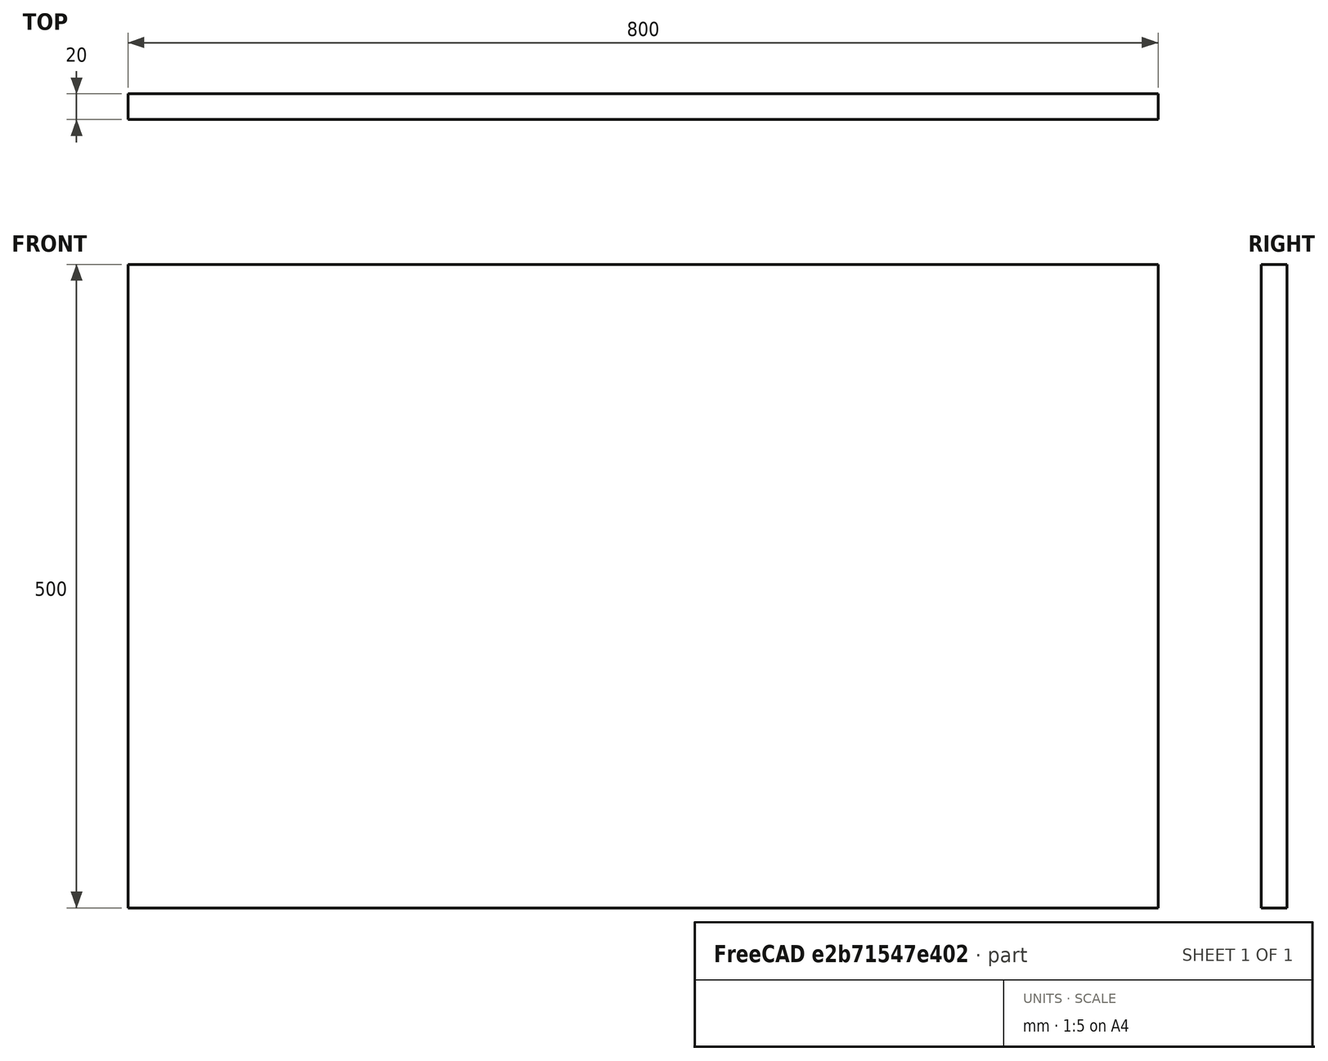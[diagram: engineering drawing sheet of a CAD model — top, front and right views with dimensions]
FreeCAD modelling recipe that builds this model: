
FCSTD DOCUMENT  (FreeCAD 0.20R29603 (Git))
Label: PlatteHinten
License: All rights reserved
LicenseURL: http://en.wikipedia.org/wiki/All_rights_reserved
objects: Sketcher::SketchObject×1, PartDesign::Pad×1, PartDesign::Body×1
note: 4 computed .brp shape members not serialized (recipe doc carries the construction recipe); baked Part::Feature solids carry a one-line shape summary decoded from their .brp

FEATURE [Sketcher::SketchObject] Sketch
  FullyConstrained = true
  MapMode = 5
  Placement = pos=(0,0,0) rot=(1,0,0;1.5708rad)
  Support = -> [XZ_Plane]
  sketch-geometry (5):
    g0: LineSegment StartX=-400 StartY=250 StartZ=0 EndX=-400 EndY=-250 EndZ=0
    g1: LineSegment StartX=-400 StartY=-250 StartZ=0 EndX=400 EndY=-250 EndZ=0
    g2: LineSegment StartX=400 StartY=-250 StartZ=0 EndX=400 EndY=250 EndZ=0
    g3: LineSegment StartX=400 StartY=250 StartZ=0 EndX=-400 EndY=250 EndZ=0
    g4: GeomPoint X=0 Y=0 Z=0
  constraints (12):
    c: Coincident(g0,g1)
    c: Coincident(g1,g2)
    c: Coincident(g2,g3)
    c: Coincident(g3,g0)
    c: Horizontal(g1)
    c: Horizontal(g3)
    c: Vertical(g0)
    c: Vertical(g2)
    c: Symmetric(g1,g0,g4)
    c: Coincident(g4,g-1)
    c: Distance(g3) = 800
    c: Distance(g0) = 500
FEATURE [PartDesign::Pad] Pad
  Direction = (0,-1,-2e-16)
  Length = 20
  Length2 = 10
  Placement = pos=(0,0,0) rot=(1,0,0;1.5708rad)
  Profile = -> Sketch
  ReferenceAxis = -> Sketch [N_Axis]
  Type = 0
FEATURE [PartDesign::Body] Body
  Group = -> [Sketch,Pad]
  Origin = -> Origin
  Tip = -> Pad
